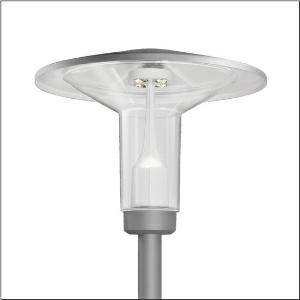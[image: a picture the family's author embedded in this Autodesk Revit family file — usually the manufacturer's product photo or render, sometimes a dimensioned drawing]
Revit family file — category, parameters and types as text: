
# Revit family: laterne_iq___p1_0a_5xa5255bf14h_d88c
name_source: partatom
category: Lighting Fixtures
units: mm (PartAtom-declared; Revit-internal decimal feet)

## family parameters
Cut with Voids When Loaded = No
Host = Face
Light Source = No
Part Type = Normal
Room Calculation Point = No
Round Connector Dimension = Use Diameter
Shared = No

## types (1)
- --- (1 x LED, 1510 lm, 12.9 W, 2200K)
    Apparent Load = 13 VA
    CIE Flux Codes = 35 64 91 96 100
    Color Rendering = 70
    Color Temperature = 2200K
    Default Elevation = 1800 mm
    Description = Lantern iQ, mast luminaire, Module 540 iQ-SR, primary light control with 3 zone facetted reflector, of plastic, silver coated, highly specular, structured, primary optical cover: cover, of PMMA, transparent, light distribution: P1.0a, light emission: direct distribution, primary light characteristic: strongly asymmetric, installation type: post-top, LED, High Power LED, rated luminous flux: 1.510lm, luminous efficacy: 117lm/W, light colour: 722, colour temperature: 2200K, control gear: ECG iQ, control: presetting dimming logarithmic, Street-Remote, Auto-Match, Temp-Guard, Lumen-Switch, Night-Set, Smart-Wire, Light-Fading, Desk-Remote (wireless, voltage-free reading and setting of iQ features in the workshop via application-optimized NFC function/RFID function), optimised constant luminous flux control (CLO 2.0), with terminal, 6-pole, max. 2.5mm², mains connection: 230..240V, AC, 50/60Hz, start of lifetime: 13W, end of service life: 13W, reduction: 6W, luminaire housing, upper part, of glass-fibre reinforced polyester, coated, Siteco® metallic grey (DB 702S), diameter: 750mm, height: 583mm, spigot size: d x l = 76 x 70mm (post-top) | with reducer (optional accessory) 60 x 70mm, post-top mast mounting element, of diecast aluminium, coated, Siteco® metallic grey (DB 702S), Module 540 iQ-SR, traffic white (RAL 9016), equipment: standard, protection rating (complete): IP65, insulation class (complete): insulation class II (safety insulation), certification: CE, ENEC, VDE, packaging unit: 1 piece

Light Distribution: P1.0a
    Height = 583 mm
    Lamp = 1 x LED
    Lamp Light Flux = 1510 lm
    Lamp Power = 12.9 W
    Lamp count = 1
    Length = 750 mm
    Luminous efficacy = 117 lm/W
    Manufacturer = Siteco
    ModVariant = No
    Model = 5XA5255BF14H
    Number of Poles = 1
    OnlyDefault = Yes
    Power Factor = 1
    Product Name = Laterne iQ | P1.0a
    Product group = mast luminaire | pylon top
    ProductGroupID = 6100
    Protection Class = Protection class II
    Protection Degree = IP 65
    RLX_Detail_Level = 1
    RLX_Emergency_Light_Flux = 0 lm
    RLX_Emergency_Type = 0
    RLX_Emergency_Type_DB = No
    RlxData = <blob elided: 74285 chars, md5=2142287d>
    Socket = socket
    Standby Power = 0 W
    System Light Flux = 1510 lm
    System Power = 13 W
    Type Comments = factory setting: luminous flux: 100 % | dim-lin: 254 | 516 mA
    Type Image = l_1006050.jpg
    URL = http://relux.com
    VarID = @adj_092861
    Voltage = 0 V
    Weight = 0.00 kg
    Width = 0 mm  [stored 0 ft]

note: [stored X ft] marks values corroborated as IEEE doubles in the binary element streams (Revit-internal decimal feet)

## geometry (parser evidence)
native form markers: Blend x4, Sweep x9
no freeform markers — native parametric forms only
